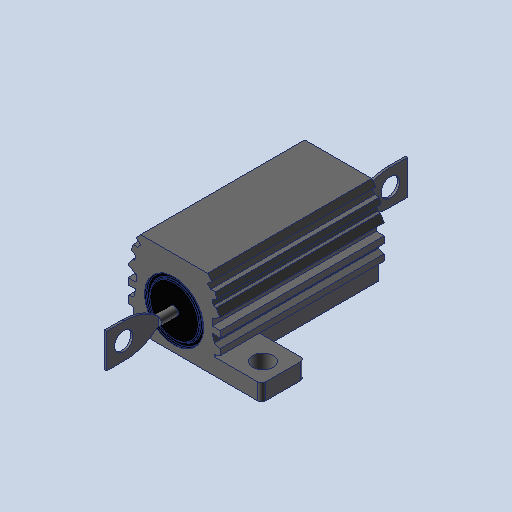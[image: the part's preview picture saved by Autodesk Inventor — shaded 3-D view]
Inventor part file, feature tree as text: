
AUTODESK INVENTOR PART (.ipt)
format: ipt  version: 2024 (Build 280153000, 153)  size: 210,432 bytes
history: native  units: in
note: dims shown in document units (in); Inventor stores cm internally (conversion verified against a paired STEP export)
features: mirror x1
ambient origin geometry x8: Origin, YZ Plane, XZ Plane, XY Plane, X Axis, Y Axis, Z Axis, Center Point
bodies: Solid1 (feature_tree)
feature tree (1):
  mirror  "Mirror3"
